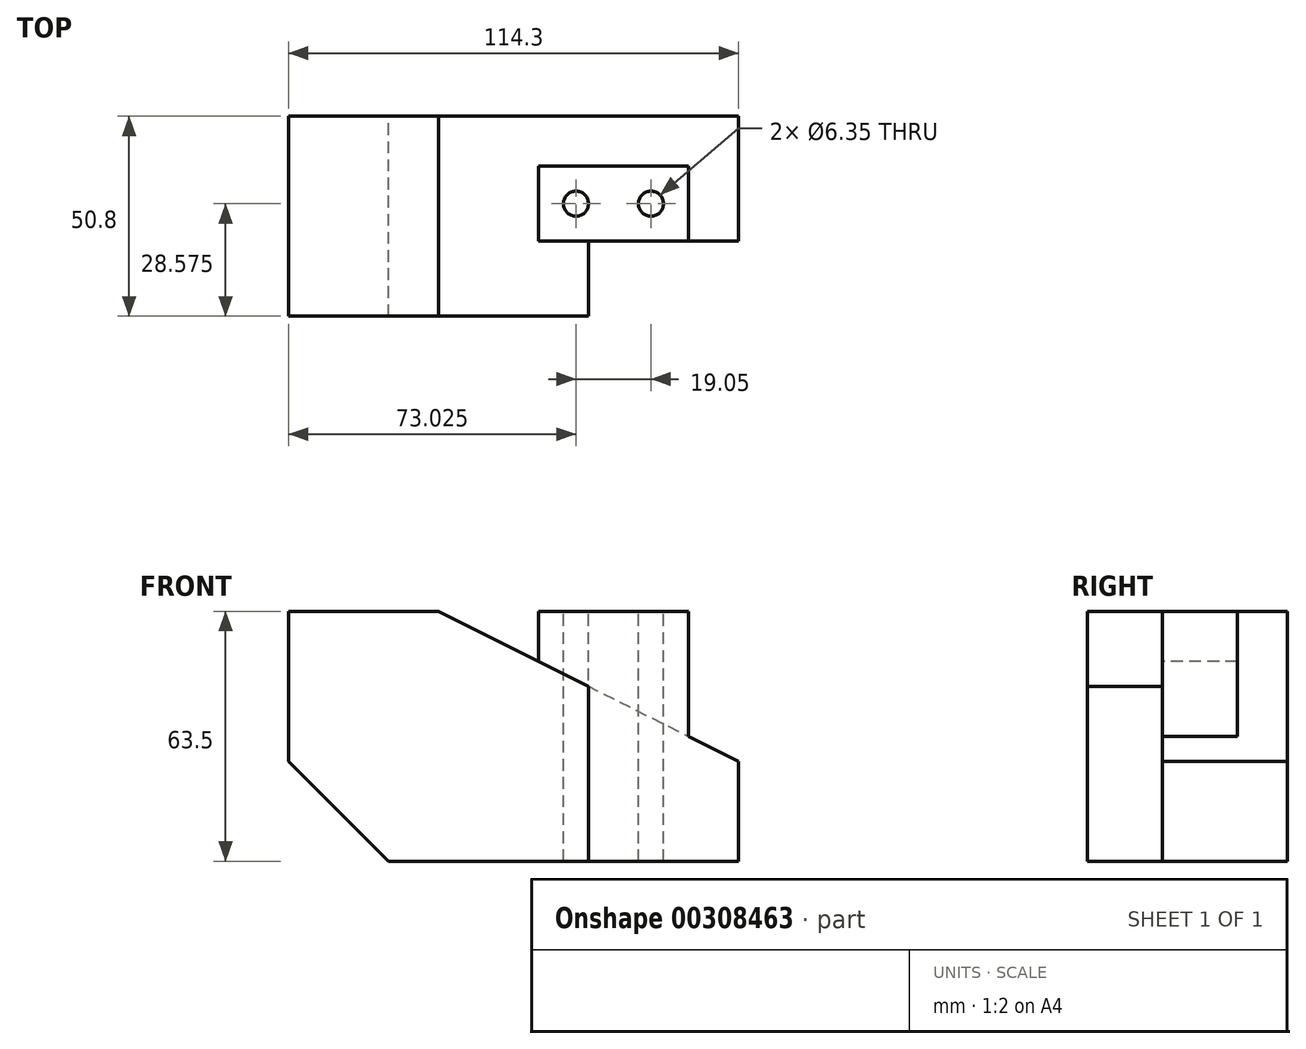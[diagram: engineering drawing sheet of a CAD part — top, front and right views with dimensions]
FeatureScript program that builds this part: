
annotation { "Feature Type Name" : "Feature", "Feature Type Description" : "" }
export const myFeature = defineFeature(function(context is Context, id is Id, definition is map)
    precondition{}
    {
        {
            var Q0;
            Q0=qCreatedBy(makeId("Front.planeOp"),FACE);
            var sketch = newSketch(context, id + "F0", { "sketchPlane" : qUnion([Q0])});
            skLineSegment(sketch, "E0", {"start": v(0, 0) * mm, "end": v(0, 38.1) * mm});
            skLineSegment(sketch, "E1", {"start": v(0, 38.1) * mm, "end": v(38.1, 38.1) * mm});
            skLineSegment(sketch, "E2", {"start": v(38.1, 38.1) * mm, "end": v(114.3, 0) * mm});
            skLineSegment(sketch, "E3", {"start": v(114.3, 0) * mm, "end": v(114.3, -25.4) * mm});
            skLineSegment(sketch, "E4", {"start": v(114.3, -25.4) * mm, "end": v(25.4, -25.4) * mm});
            skLineSegment(sketch, "E5", {"start": v(25.4, -25.4) * mm, "end": v(0, 0) * mm});
            skLineSegment(sketch, "E6", {"start": v(76.2, 19.05) * mm, "end": v(76.2, -25.4) * mm});
            skSolve(sketch);
        }
        {
            var Q0;
            Q0=makeQuery(id+"F0.imprint","IMPRINT",FACE,{"disambiguationData":[TD([[makeQuery(id+"F0.imprint","IMPRINT",EDGE,{"derivedFrom":sQuery(id+"F0.wireOp",EDGE,"E0")}),-1.0]])]});
            extrude(context, id + "F1", {"entities" : qUnion([Q0]), "depth" : 50.8 * mm});
        }
        {
            var Q0;
            {var subQ0=sQuery(id+"F0.wireOp",EDGE,"E3");Q0=makeQuery(id+"F0.imprint","IMPRINT",FACE,{"disambiguationData":[TD([[makeQuery(id+"F0.imprint","IMPRINT",EDGE,{"derivedFrom":subQ0}),-1.0]])]});}
            extrude(context, id + "F2", {"entities" : qUnion([Q0]), "operationType" : NewBodyOperationType.ADD, "depth" : 31.75 * mm});
        }
        {
            var Q0;
            Q0=makeQuery(id+"F2.opExtrude","CAP_FACE",FACE,{"disambiguationData":[OSD([sQuery(id+"F0.wireOp",EDGE,"E2"),sQuery(id+"F0.wireOp",EDGE,"E3"),sQuery(id+"F0.wireOp",EDGE,"E4"),sQuery(id+"F0.wireOp",EDGE,"E6")])],"isStart":false});
            var sketch = newSketch(context, id + "F3", { "sketchPlane" : qUnion([Q0])});
            skLineSegment(sketch, "E7", {"start": v(76.2, -25.4) * mm, "end": v(101.6, -25.4) * mm});
            skLineSegment(sketch, "E8", {"start": v(101.6, -25.4) * mm, "end": v(101.6, 38.1) * mm});
            skLineSegment(sketch, "E9", {"start": v(101.6, 38.1) * mm, "end": v(63.5, 38.1) * mm});
            skLineSegment(sketch, "E10", {"start": v(63.5, 38.1) * mm, "end": v(63.5, 25.4) * mm});
            skLineSegment(sketch, "E11", {"start": v(63.5, 25.4) * mm, "end": v(76.2, 19.05) * mm});
            skLineSegment(sketch, "E12", {"start": v(76.2, 19.05) * mm, "end": v(76.2, -25.4) * mm});
            skSolve(sketch);
        }
        {
            var Q0;
            Q0 = qSketchRegion(id + "F3", true);
            extrude(context, id + "F4", {"entities" : qUnion([Q0]), "operationType" : NewBodyOperationType.ADD, "oppositeDirection" : true, "depth" : 19.05 * mm});
        }
        {
            var Q0;
            Q0=makeQuery(id+"F4.opExtrude","SWEPT_FACE",FACE,{"disambiguationData":[OSD([sQuery(id+"F3.wireOp",EDGE,"E9")])]});
            var sketch = newSketch(context, id + "F5", { "sketchPlane" : qUnion([Q0])});
            skCircle(sketch, "E13", {"center": v(73.03, -22.23) * mm, "radius": 3.18 * mm});
            skCircle(sketch, "E14", {"center": v(92.07, -22.23) * mm, "radius": 3.18 * mm});
            skLineSegment(sketch, "E15", {"start": v(101.6, -22.22) * mm, "end": v(63.5, -22.22) * mm, "construction": true});
            skSolve(sketch);
        }
        {
            var Q0;
            Q0 = qSketchRegion(id + "F5", true);
            extrude(context, id + "F6", {"entities" : qUnion([Q0]), "operationType" : NewBodyOperationType.REMOVE, "endBound" : BoundingType.THROUGH_ALL, "oppositeDirection" : true, "depth" : 25.4 * mm});
        }
    });
